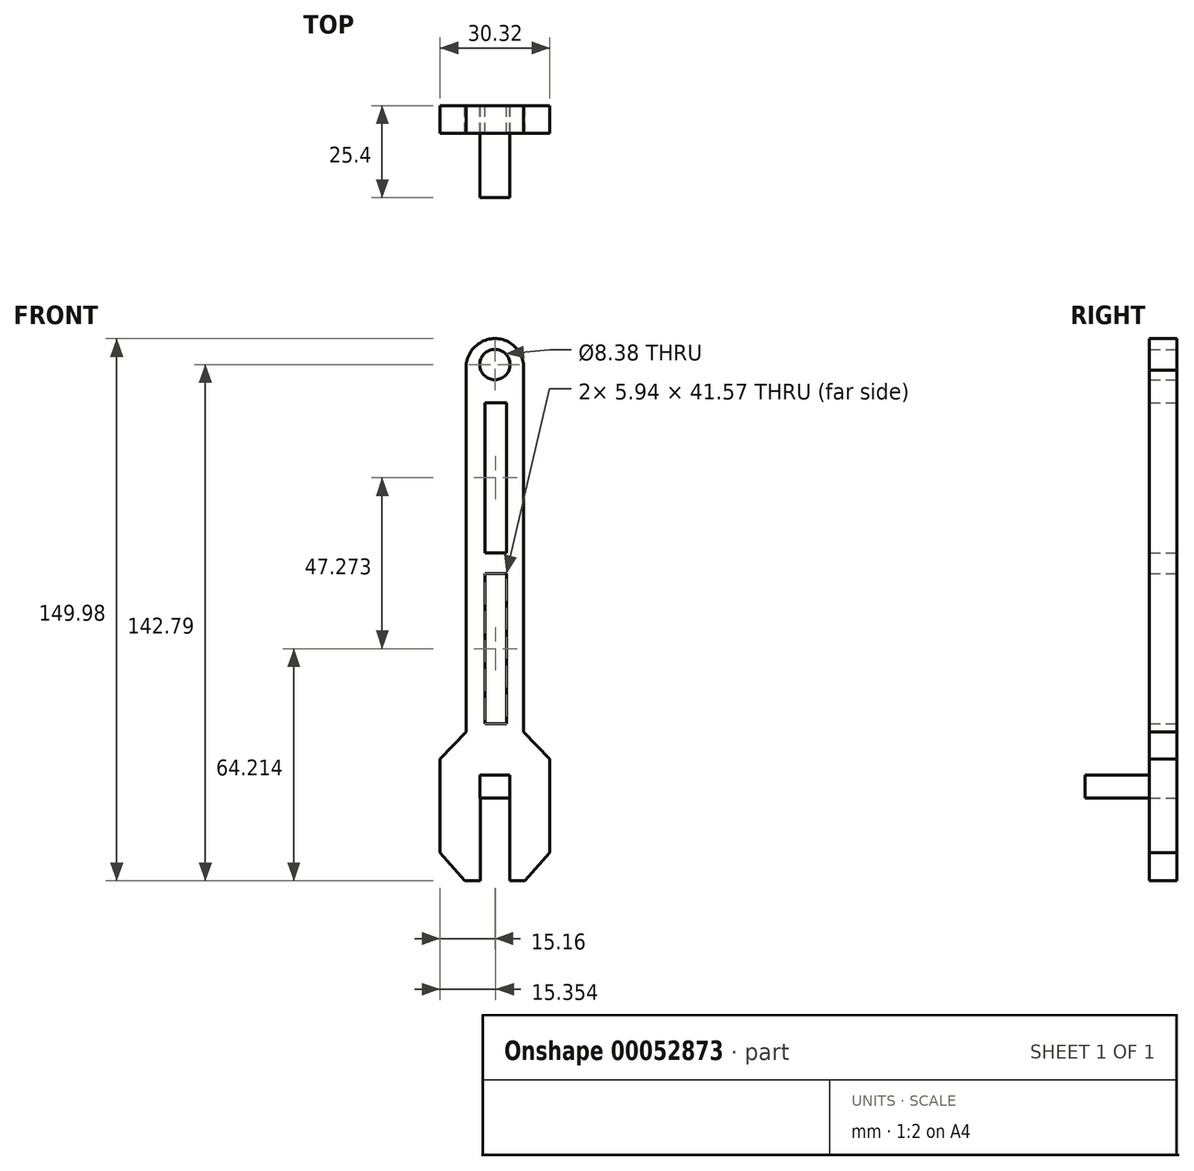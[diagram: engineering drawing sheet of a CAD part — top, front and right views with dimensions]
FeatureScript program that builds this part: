
annotation { "Feature Type Name" : "Feature", "Feature Type Description" : "" }
export const myFeature = defineFeature(function(context is Context, id is Id, definition is map)
    precondition{}
    {
        {
            var Q0;
            Q0=qCreatedBy(makeId("Front.planeOp"),FACE);
            var sketch = newSketch(context, id + "F0", { "sketchPlane" : qUnion([Q0])});
            skLineSegment(sketch, "E0", {"start": v(-8.35, -41.19) * mm, "end": v(-15.16, -33.4) * mm});
            skLineSegment(sketch, "E1", {"start": v(-15.16, -33.4) * mm, "end": v(-15.16, -7.47) * mm});
            skLineSegment(sketch, "E2", {"start": v(-15.16, -7.47) * mm, "end": v(-7.9, 0) * mm});
            skLineSegment(sketch, "E3", {"start": v(-4.06, -41.19) * mm, "end": v(-4.06, -18.33) * mm});
            skLineSegment(sketch, "E4", {"start": v(-4.06, -18.33) * mm, "end": v(4.06, -18.33) * mm});
            skLineSegment(sketch, "E5", {"start": v(-7.9, 0) * mm, "end": v(-7.9, 101.6) * mm});
            skLineSegment(sketch, "E6.MirrorCS", {"start": v(4.06, -41.19) * mm, "end": v(4.06, -18.33) * mm});
            skLineSegment(sketch, "E7.MirrorCS", {"start": v(8.35, -41.19) * mm, "end": v(15.16, -33.4) * mm});
            skLineSegment(sketch, "E8.MirrorCS", {"start": v(15.16, -33.4) * mm, "end": v(15.16, -7.47) * mm});
            skLineSegment(sketch, "E9.MirrorCS", {"start": v(15.16, -7.47) * mm, "end": v(7.9, 0) * mm});
            skLineSegment(sketch, "E10", {"start": v(4.06, -41.19) * mm, "end": v(8.35, -41.19) * mm});
            skLineSegment(sketch, "E11", {"start": v(-8.35, -41.19) * mm, "end": v(-4.06, -41.19) * mm});
            skArc(sketch, "E12", {"start": v(7.9, 100.1) * mm, "mid": v(0, 108.8) * mm, "end": v(-7.9, 100.1) * mm});
            skPoint(sketch, "E12.third.point", {"position": v(1.47, 108.66) * mm});
            skCircle(sketch, "E13", {"center": v(0, 101.6) * mm, "radius": 4.2 * mm});
            skLineSegment(sketch, "E14", {"start": v(7.9, 100.1) * mm, "end": v(7.9, 0) * mm});
            skLineSegment(sketch, "E15.bottom", {"start": v(-2.78, 91.08) * mm, "end": v(3.16, 91.08) * mm});
            skLineSegment(sketch, "E15.top", {"start": v(-2.78, 49.51) * mm, "end": v(3.16, 49.51) * mm});
            skLineSegment(sketch, "E15.left", {"start": v(-2.78, 91.08) * mm, "end": v(-2.78, 49.51) * mm});
            skLineSegment(sketch, "E15.right", {"start": v(3.16, 91.08) * mm, "end": v(3.16, 49.51) * mm});
            skLineSegment(sketch, "E16.MirrorCS", {"start": v(-2.78, 2.24) * mm, "end": v(-2.78, 43.8) * mm});
            skLineSegment(sketch, "E17.MirrorCS", {"start": v(-2.78, 2.24) * mm, "end": v(3.16, 2.24) * mm});
            skLineSegment(sketch, "E18.MirrorCS", {"start": v(3.16, 2.24) * mm, "end": v(3.16, 43.8) * mm});
            skLineSegment(sketch, "E19.MirrorCS", {"start": v(-2.78, 43.8) * mm, "end": v(3.16, 43.8) * mm});
            skSolve(sketch);
        }
        {
            var Q0;
            Q0 = qSketchRegion(id + "F0", true);
            extrude(context, id + "F1", {"entities" : qUnion([Q0]), "depth" : 7.62 * mm});
        }
        {
            var Q0;
            Q0=qCreatedBy(makeId("Front.planeOp"),FACE);
            var sketch = newSketch(context, id + "F2", { "sketchPlane" : qUnion([Q0])});
            skLineSegment(sketch, "E20.bottom", {"start": v(-4.09, -18.33) * mm, "end": v(4.08, -18.33) * mm});
            skLineSegment(sketch, "E20.top", {"start": v(-4.09, -11.96) * mm, "end": v(4.08, -11.96) * mm});
            skLineSegment(sketch, "E20.left", {"start": v(-4.09, -18.33) * mm, "end": v(-4.09, -11.96) * mm});
            skLineSegment(sketch, "E20.right", {"start": v(4.08, -18.33) * mm, "end": v(4.08, -11.96) * mm});
            skSolve(sketch);
        }
        {
            var Q0;
            Q0 = qSketchRegion(id + "F2", true);
            extrude(context, id + "F3", {"entities" : qUnion([Q0]), "operationType" : NewBodyOperationType.ADD, "depth" : 25.4 * mm});
        }
    });
